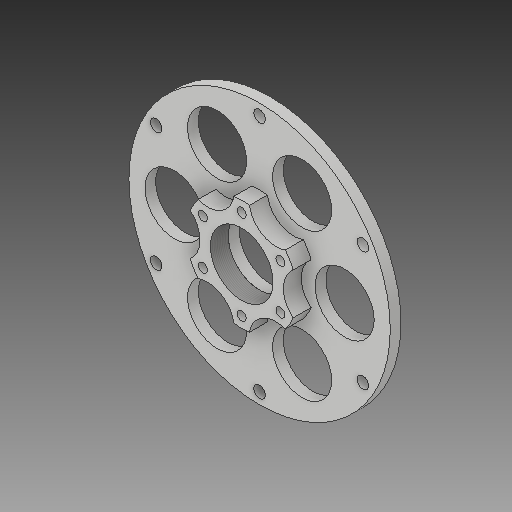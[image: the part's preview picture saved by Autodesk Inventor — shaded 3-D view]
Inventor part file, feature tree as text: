
AUTODESK INVENTOR PART (.ipt)
format: ipt  version: 2019.3 (Build 233278000, 278)  size: 225,280 bytes
history: native  units: mm
features: other x2, sketch x2, extrude x2, hole x2, thread x1
ambient origin geometry x8: Origin, YZ Plane, XZ Plane, XY Plane, X Axis, Y Axis, Z Axis, Center Point
bodies: Body1 (feature_tree), Body2 (feature_tree)
feature tree (9):
  other  "SprocketHubPlate"
  sketch  "Sketch1"  dims[d0=66.675mm d1=60.0mm d3=360.0deg]
  extrude  "Extrusion2"  Depth=60.0mm TaperAngle=360.0deg
  hole  "Hole2"  [1 undecoded]
  hole  "Hole3"  [1 undecoded]
  extrude  "Extrusion3"  Depth=10.0mm TaperAngle=360.0deg
  thread  "Thread1"  [1 undecoded]
  sketch  "Sketch3"  dims[d9=35.0mm d19=33.0mm d20=25.0mm d21=60.0mm d23=360.0deg d25=146.0mm d26=60.0mm d28=360.0deg d30=6.0mm d31=0.0mm d32=6.5mm d33=6.0mm d34=4.0mm d35=2.0mm d36=90.0deg d37=8.0mm d38=20.594885mm d39=5.0mm d40=6.0mm d41=4.0mm d42=2.0mm d43=90.0deg d44=8.0mm d45=20.594885mm d46=62.0mm d48=60.0deg d49=30.0mm d50=60.0mm d52=360.0deg d54=10.0mm d55=0.0mm d56=10.0mm d57=0.0mm d12=1.0mm d13=1.0mm]
  other  "ScrewAdapterPlate"
note: 3 required parameter values undecoded (feature->parameter linkage not recoverable at this tier; creation-order binding heuristic only, values carry confidence <= 0.55)
